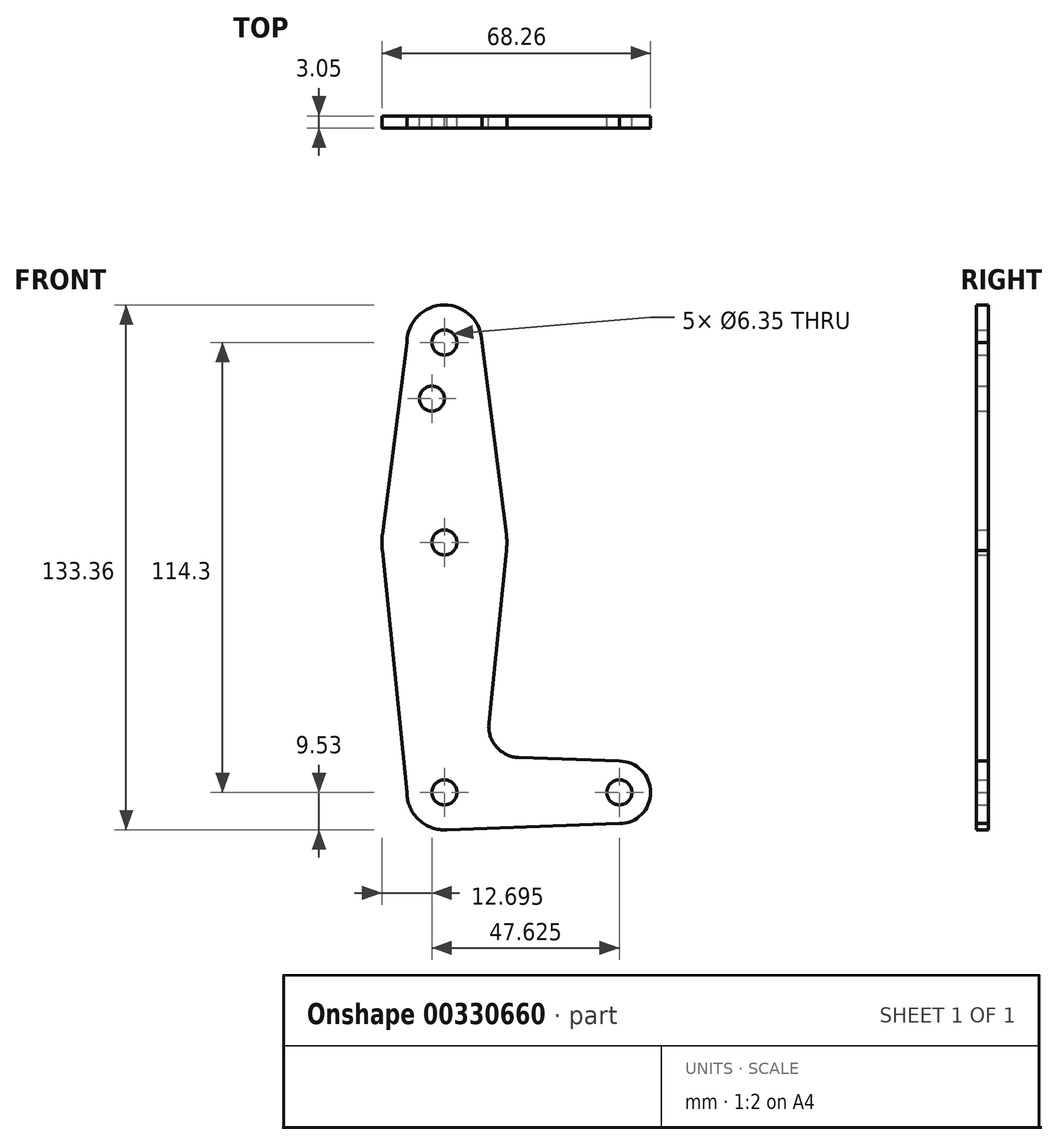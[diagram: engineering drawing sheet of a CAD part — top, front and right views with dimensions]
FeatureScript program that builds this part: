
annotation { "Feature Type Name" : "Feature", "Feature Type Description" : "" }
export const myFeature = defineFeature(function(context is Context, id is Id, definition is map)
    precondition{}
    {
        {
            var Q0;
            Q0=qCreatedBy(makeId("Front.planeOp"),FACE);
            var sketch = newSketch(context, id + "F0", { "sketchPlane" : qUnion([Q0])});
            skLineSegment(sketch, "E0", {"start": v(0, 0) * mm, "end": v(0, 114.3) * mm});
            skLineSegment(sketch, "E1", {"start": v(0, 0) * mm, "end": v(44.45, 0) * mm});
            skCircle(sketch, "E2", {"center": v(0, 114.3) * mm, "radius": 9.53 * mm});
            skCircle(sketch, "E3", {"center": v(0, 63.5) * mm, "radius": 15.88 * mm});
            skCircle(sketch, "E4", {"center": v(0, 0) * mm, "radius": 9.53 * mm});
            skCircle(sketch, "E5", {"center": v(44.45, 0) * mm, "radius": 7.94 * mm});
            skLineSegment(sketch, "E6", {"start": v(18.93, 8.85) * mm, "end": v(44.45, 7.94) * mm});
            skLineSegment(sketch, "E7", {"start": v(0, -9.52) * mm, "end": v(44.45, -7.94) * mm});
            skCircle(sketch, "E8", {"center": v(0, 114.3) * mm, "radius": 3.18 * mm});
            skCircle(sketch, "E9", {"center": v(0, 63.5) * mm, "radius": 3.18 * mm});
            skCircle(sketch, "E10", {"center": v(44.45, 0) * mm, "radius": 3.18 * mm});
            skCircle(sketch, "E11", {"center": v(0, 0) * mm, "radius": 3.18 * mm});
            skLineSegment(sketch, "E12", {"start": v(-9.53, 114.3) * mm, "end": v(-15.75, 65.5) * mm});
            skLineSegment(sketch, "E13", {"start": v(-15.75, 65.5) * mm, "end": v(-15.75, 61.5) * mm});
            skLineSegment(sketch, "E14", {"start": v(-15.75, 61.5) * mm, "end": v(-9.53, 0) * mm});
            skLineSegment(sketch, "E15", {"start": v(9.53, 114.3) * mm, "end": v(15.75, 65.5) * mm});
            skLineSegment(sketch, "E16", {"start": v(11.3, 17.6) * mm, "end": v(15.75, 61.5) * mm});
            skCircle(sketch, "E17", {"center": v(-3.18, 100.03) * mm, "radius": 3.18 * mm});
            skPoint(sketch, "E18.newPointB", {"position": v(9.53, 0) * mm});
            skArc(sketch, "E18.filletArc", {"start": v(11.3, 17.6) * mm, "mid": v(13.22, 11.57) * mm, "end": v(18.93, 8.85) * mm});
            skSolve(sketch);
        }
        {
            var Q0;
            Q0 = qSketchRegion(id + "F0", true);
            var Q1;
            {var subQ0=sQuery(id+"F0.wireOp",EDGE,"E11");var subQ1=sQuery(id+"F0.wireOp",EDGE,"E0");var subQ2=makeQuery(id+"F0.imprint","INTERSECT",VERTEX,{"derivedFrom":[subQ1,subQ0]});Q1=makeQuery(id+"F0.imprint","IMPRINT",FACE,{"disambiguationData":[TD([[makeQuery(id+"F0.imprint","IMPRINT",EDGE,{"disambiguationData":[TD([[subQ2,-1.0]])],"derivedFrom":subQ1}),-1.0]])]});}
            extrude(context, id + "F1", {"entities" : qUnion([Q0, Q1]), "depth" : 3.05 * mm});
        }
    });
